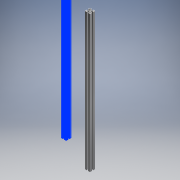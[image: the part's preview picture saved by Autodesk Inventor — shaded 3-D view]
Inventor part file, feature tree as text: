
AUTODESK INVENTOR PART (.ipt)
format: ipt  version: 2019 (Build 230136000, 136)  size: 318,976 bytes
history: native  units: mm
features: other x1, extrude x1, fillet x1, sketch x1
ambient origin geometry x8: Origin, YZ Plane, XZ Plane, XY Plane, X Axis, Y Axis, Z Axis, Center Point
bodies: Body1 (feature_tree)
feature tree (4):
  other  "솔리드1"
  extrude  "돌출1"  Depth=30.0mm
  fillet  "모깎기1"  Radius=30.0mm
  sketch  "스케치1"
